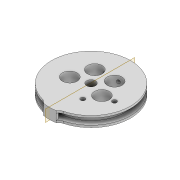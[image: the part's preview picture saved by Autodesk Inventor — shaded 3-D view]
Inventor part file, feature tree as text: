
AUTODESK INVENTOR PART (.ipt)
format: ipt  version: 2022 (Build 260153000, 153)  size: 281,088 bytes
history: native  units: mm
features: extrude x8, sketch x7, plane x3, fillet x2, pattern_circular x1, mirror x1, projected_geometry x1
ambient origin geometry x8: Origin, YZ Plane, XZ Plane, XY Plane, X Axis, Y Axis, Z Axis, Center Point
bodies: Solid1 (feature_tree)
feature tree (23):
  extrude  "Extrusion1"  Depth=32.0mm
  extrude  "Extrusion2"  Depth=3.0mm TaperAngle=0.0deg
  pattern_circular  "Circular Pattern1"  Count=5 Angle=360.0deg
  plane  "Work Plane1"
  plane  "Work Plane2"
  extrude  "Extrusion3"  [1 undecoded]
  extrude  "Extrusion4"  Depth=5.0mm
  fillet  "Fillet1"  Radius=2.5mm
  plane  "Work Plane3"
  extrude  "Extrusion5"  Depth=5.0mm TaperAngle=0.0deg
  mirror  "Mirror1"
  sketch  "Sketch6"  dims[d13=9.599311mm d14=-9.599311mm]
  extrude  "Extrusion6"  Depth=5.0mm
  extrude  "Extrusion7"  Depth=5.0mm
  extrude  "Extrusion8"  Depth=5.0mm
  fillet  "Fillet2"  Radius=10.0mm
  sketch  "Sketch1"  dims[d0=4.2mm d2=32.0mm]
  sketch  "Sketch2"  dims[d3=4.0mm d4=3.0mm d5=0.0mm]
  sketch  "Sketch3"  dims[d6=7.0mm]
  sketch  "Sketch4"  dims[d7=8.0mm]
  sketch  "Sketch5"  dims[d8=10.0mm d9=0.0mm d10=50.0mm d11=360.0deg]
  projected_geometry  "Projected Loop1"
  sketch  "Sketch7"  dims[d15=1.5mm d16=1.5mm d17=2.5mm d18=5.0mm d19=0.0mm d20=1.5mm d21=1.5mm d22=2.5mm d23=10.0mm d24=0.0mm d25=1.0mm d26=37.4mm d27=1.0mm d28=0.0mm d29=2.1mm d30=13.0mm d31=1.9mm d32=2.1mm d33=8.4mm d35=5.0mm d36=0.0mm d37=100.0mm d38=0.0mm d39=4.5mm d40=3.0mm d41=3.0mm d42=1.0mm d43=5.0mm d44=0.0mm d45=3.0mm d46=10.0mm d47=0.0mm d48=5.0mm d49=0.0mm]
note: 1 required parameter value undecoded (feature->parameter linkage not recoverable at this tier; creation-order binding heuristic only, values carry confidence <= 0.55)
